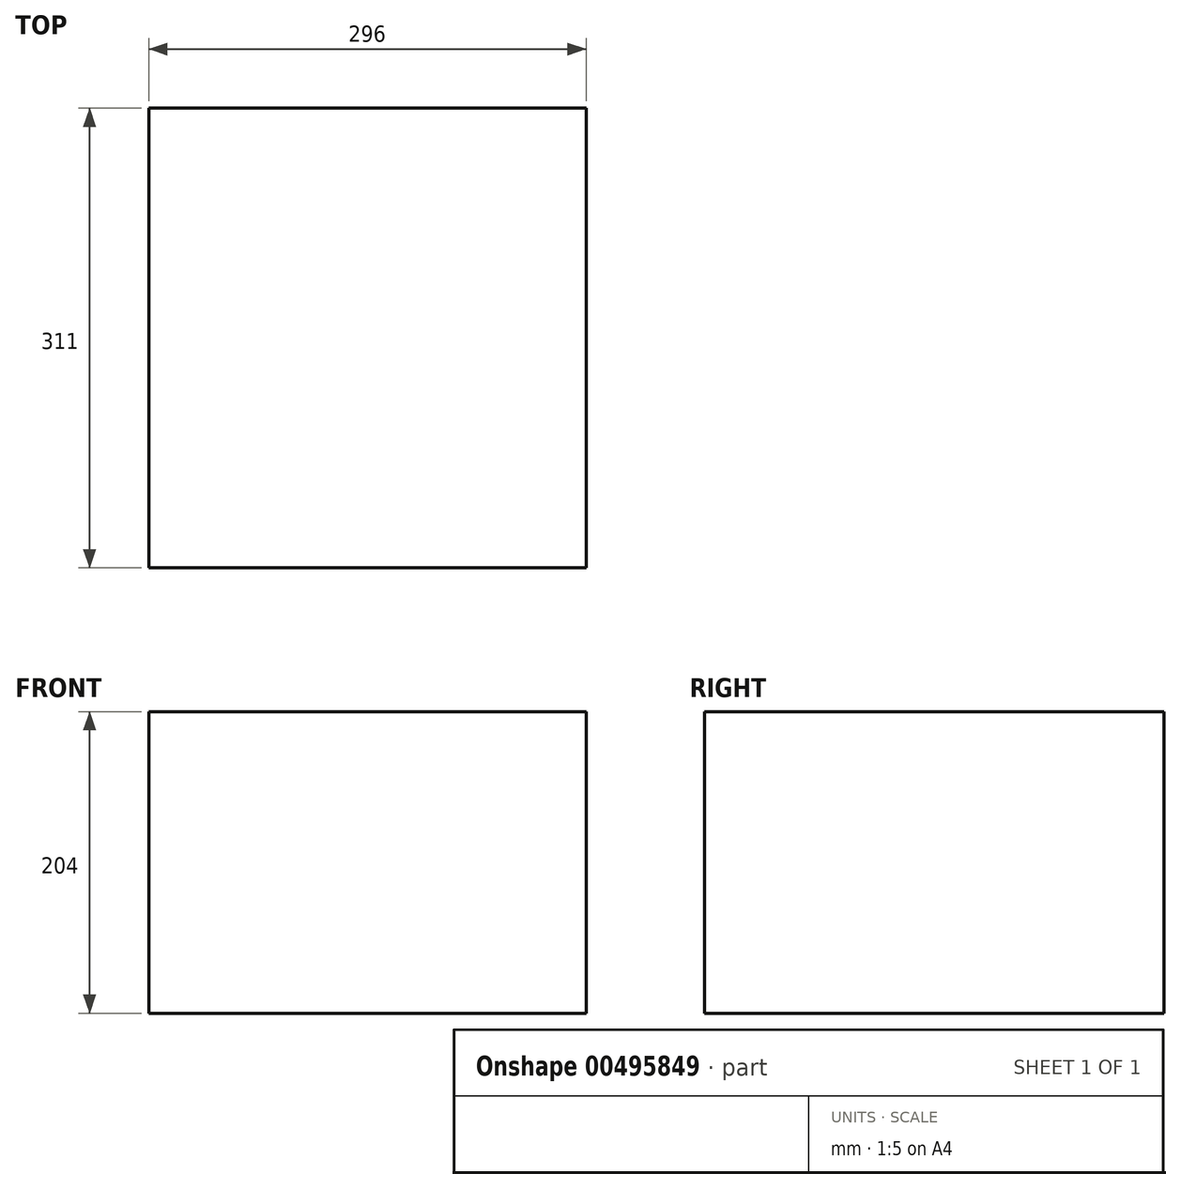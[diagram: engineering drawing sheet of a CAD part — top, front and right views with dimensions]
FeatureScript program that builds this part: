
annotation { "Feature Type Name" : "Feature", "Feature Type Description" : "" }
export const myFeature = defineFeature(function(context is Context, id is Id, definition is map)
    precondition{}
    {
        {
            var Q0;
            Q0=qCreatedBy(makeId("Front.planeOp"),FACE);
            var sketch = newSketch(context, id + "F0", { "sketchPlane" : qUnion([Q0])});
            skLineSegment(sketch, "E0.bottom", {"start": v(148, 102) * mm, "end": v(-148, 102) * mm});
            skLineSegment(sketch, "E0.top", {"start": v(148, -102) * mm, "end": v(-148, -102) * mm});
            skLineSegment(sketch, "E0.left", {"start": v(148, 102) * mm, "end": v(148, -102) * mm});
            skLineSegment(sketch, "E0.right", {"start": v(-148, 102) * mm, "end": v(-148, -102) * mm});
            skPoint(sketch, "E0.middle", {"position": v(0, 0) * mm});
            skSolve(sketch);
        }
        {
            var Q0;
            Q0=qSketchRegion(id+"F0",true);
            extrude(context, id + "F1", {"entities" : qUnion([Q0]), "depth" : 311 * mm});
        }
    });
